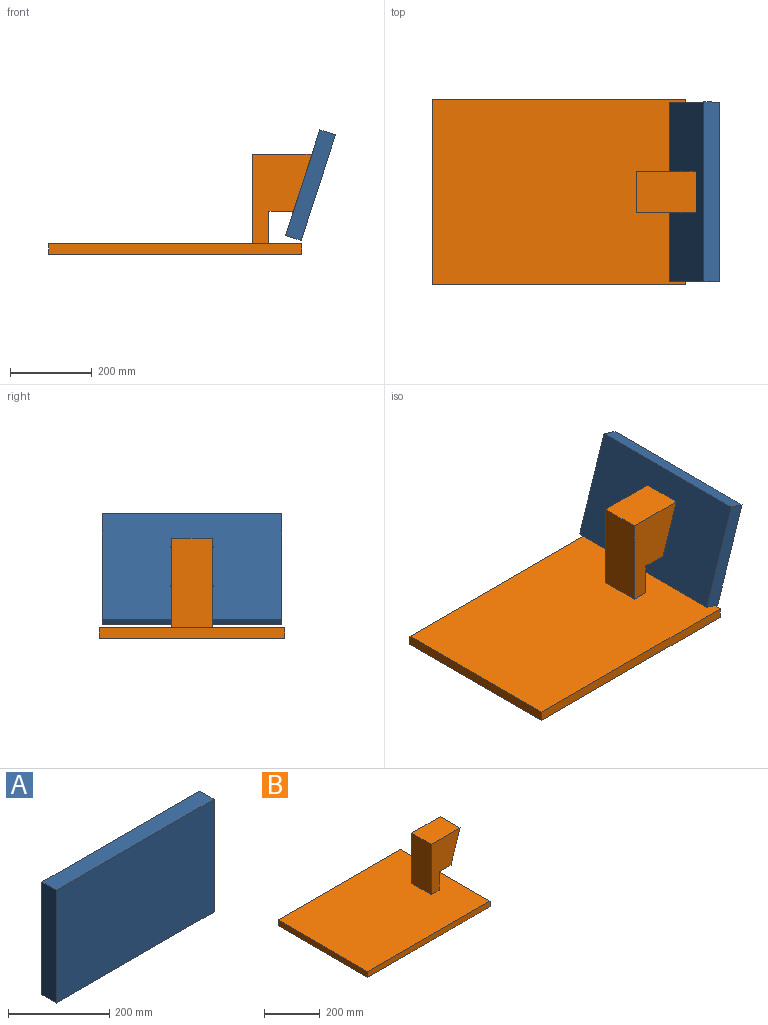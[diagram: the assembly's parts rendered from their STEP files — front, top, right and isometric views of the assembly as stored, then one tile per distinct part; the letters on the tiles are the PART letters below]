
ASSEMBLY  parts=2 mates=1
PART A: 14 faces, bbox 440x40x272 mm
  f0: plane 272x40mm, normal (-1,0,0), area 10880mm2, adj f1,f3,f4,f5
  f1: plane 440x40mm, normal (0,0,-1), area 17600mm2, adj f0,f2,f4,f5
  f2: plane 272x40mm, normal (1,0,0), area 10880mm2, adj f1,f3,f4,f5
  f3: plane 440x40mm, normal (0,0,1), area 17600mm2, adj f0,f2,f4,f5
  f4: plane 440x272mm, normal (0,-1,0), area 119680mm2, adj f0,f1,f2,f3
  f5: plane 440x272mm, normal (0,1,0), area 119619.2mm2, adj f0,f1,f2,f3,f6,f8,f10,f12
  f6: cylinder r=2.2mm len=10mm, axis (0,1,0), area 138.2mm2, adj f5,f7
  f7: cone r=0mm half-angle=59deg, axis (0,1,0), area 17.7mm2, adj f6
  f8: cylinder r=2.2mm len=10mm, axis (0,1,0), area 138.2mm2, adj f5,f9
  f9: cone r=0mm half-angle=59deg, axis (0,1,0), area 17.7mm2, adj f8
  f10: cylinder r=2.2mm len=10mm, axis (0,1,0), area 138.2mm2, adj f5,f11
  f11: cone r=0mm half-angle=59deg, axis (0,1,0), area 17.7mm2, adj f10
  f12: cylinder r=2.2mm len=10mm, axis (0,1,0), area 138.2mm2, adj f5,f13
  f13: cone r=0mm half-angle=59deg, axis (0,1,0), area 17.7mm2, adj f12
PART B: 13 faces, bbox 645.5x455x245 mm
  f0: plane 620x25mm, normal (0,-1,0), area 15500mm2, adj f1,f3,f4,f5
  f1: plane 455x25mm, normal (1,0,0), area 11375mm2, adj f0,f2,f4,f5
  f2: plane 620x25mm, normal (0,1,0), area 15500mm2, adj f1,f3,f4,f5
  f3: plane 455x25mm, normal (-1,0,0), area 11375mm2, adj f0,f2,f4,f5
  f4: plane 620x455mm, normal (0,0,-1), area 282100mm2, adj f0,f1,f2,f3
  f5: plane 620x455mm, normal (0,0,1), area 278100mm2, adj f0,f1,f2,f3,f6,f7,f8,f9
  f6: plane 100x80mm, normal (1,0,0), area 8000mm2, adj f5,f7,f9,f11
  f7: plane 220x145.49mm, normal (0,1,0), area 20384.2mm2, adj f5,f6,f8,f10,f11,f12
  f8: plane 220x100mm, normal (-1,0,0), area 22000mm2, adj f5,f7,f9,f10
  f9: plane 220x145.49mm, normal (0,-1,0), area 20384.2mm2, adj f5,f6,f8,f10,f11,f12
  f10: plane 145.49x100mm, normal (0,0,1), area 14548.9mm2, adj f7,f8,f9,f12
  f11: plane 100x60mm, normal (0,0,-1), area 6000mm2, adj f6,f7,f9,f12
  f12: plane 140x100mm, normal (0.95,0,-0.31), area 14720.5mm2, adj f7,f9,f10,f11
PLACE A rot(axis=(0.15,0.15,0.98),91.4deg) t=(2.74,0,140)mm
PLACE B t=(0,0,-10)mm
MATE fastened A.f5 <-> B.f12  axis (-0.95,0,0.31) through (2.74,0,140)mm
